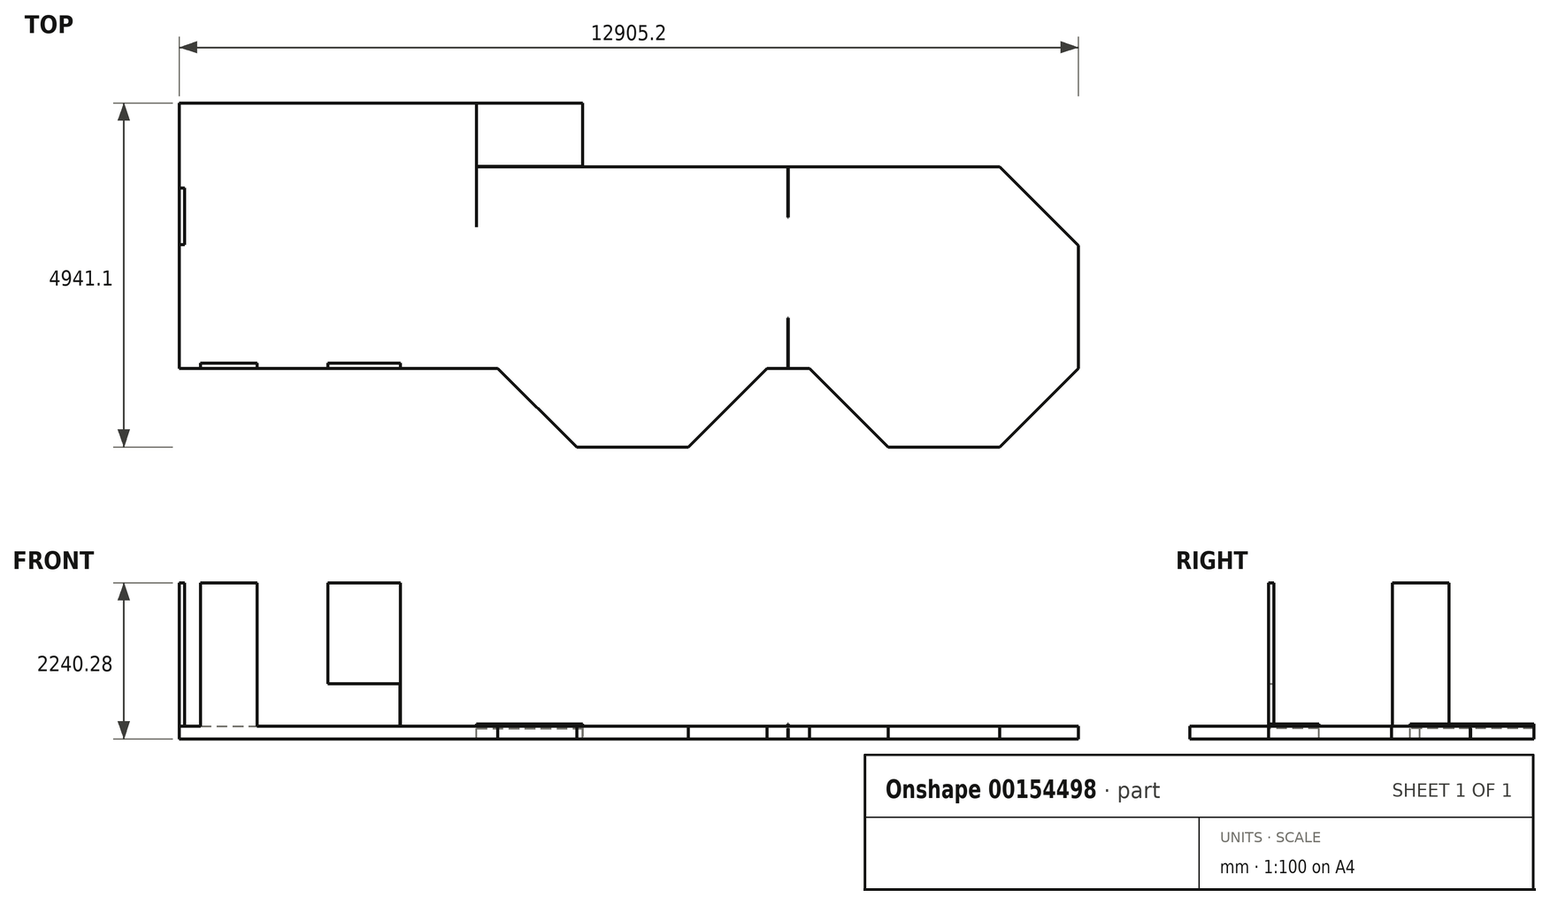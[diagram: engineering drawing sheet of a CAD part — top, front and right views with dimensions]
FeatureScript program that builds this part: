
annotation { "Feature Type Name" : "Feature", "Feature Type Description" : "" }
export const myFeature = defineFeature(function(context is Context, id is Id, definition is map)
    precondition{}
    {
        {
            var Q0;
            Q0=qCreatedBy(makeId("Top.planeOp"),FACE);
            var sketch = newSketch(context, id + "F0", { "sketchPlane" : qUnion([Q0])});
            skLineSegment(sketch, "E0", {"start": v(0, 0) * mm, "end": v(0, 3810) * mm});
            skLineSegment(sketch, "E1", {"start": v(0, 3810) * mm, "end": v(4267.2, 3810) * mm});
            skLineSegment(sketch, "E2", {"start": v(4267.2, 3810) * mm, "end": v(4267.2, 2029.97) * mm});
            skLineSegment(sketch, "E3", {"start": v(4267.2, 2029.97) * mm, "end": v(3352.8, 2029.97) * mm});
            skLineSegment(sketch, "E4", {"start": v(3352.8, 2029.97) * mm, "end": v(3352.8, 0) * mm});
            skLineSegment(sketch, "E5", {"start": v(3352.8, 0) * mm, "end": v(0, 0) * mm});
            skLineSegment(sketch, "E6", {"start": v(4267.2, 3810) * mm, "end": v(5791.2, 3810) * mm});
            skLineSegment(sketch, "E7", {"start": v(5791.2, 3810) * mm, "end": v(5791.2, 2895.6) * mm});
            skLineSegment(sketch, "E8", {"start": v(5791.2, 2895.6) * mm, "end": v(4267.2, 2895.6) * mm});
            skLineSegment(sketch, "E9", {"start": v(0, 3200.4) * mm, "end": v(3352.8, 3200.4) * mm});
            skLineSegment(sketch, "E10", {"start": v(3352.8, 3200.4) * mm, "end": v(3352.8, 3810) * mm});
            skLineSegment(sketch, "E11", {"start": v(4267.2, 2029.97) * mm, "end": v(4267.2, 0) * mm});
            skLineSegment(sketch, "E12", {"start": v(8698.45, 2171.7) * mm, "end": v(8778.78, 2171.7) * mm});
            skLineSegment(sketch, "E13", {"start": v(8778.78, 2171.7) * mm, "end": v(8778.78, 723.9) * mm});
            skLineSegment(sketch, "E14", {"start": v(8778.78, 723.9) * mm, "end": v(8698.45, 723.9) * mm});
            skLineSegment(sketch, "E15", {"start": v(8698.45, 723.9) * mm, "end": v(8698.45, 2171.7) * mm});
            skLineSegment(sketch, "E16", {"start": v(8738.62, 2895.6) * mm, "end": v(11774.13, 2895.6) * mm});
            skLineSegment(sketch, "E17", {"start": v(11774.13, 2895.6) * mm, "end": v(12905.23, 1764.5) * mm});
            skLineSegment(sketch, "E18", {"start": v(12905.23, 1764.5) * mm, "end": v(12905.23, 0) * mm});
            skLineSegment(sketch, "E19", {"start": v(12905.23, 0) * mm, "end": v(11774.13, -1131.1) * mm});
            skLineSegment(sketch, "E20", {"start": v(11774.13, -1131.1) * mm, "end": v(10174.52, -1131.1) * mm});
            skLineSegment(sketch, "E21", {"start": v(8738.62, 0) * mm, "end": v(9043.42, 0) * mm});
            skLineSegment(sketch, "E22", {"start": v(9043.42, 0) * mm, "end": v(10174.52, -1131.1) * mm});
            skLineSegment(sketch, "E23", {"start": v(5791.2, 2895.6) * mm, "end": v(8738.62, 2895.6) * mm});
            skLineSegment(sketch, "E24", {"start": v(4267.2, 0) * mm, "end": v(4572, 0) * mm});
            skLineSegment(sketch, "E25", {"start": v(8738.62, 0) * mm, "end": v(8433.82, 0) * mm});
            skLineSegment(sketch, "E26", {"start": v(4572, 0) * mm, "end": v(5703.1, -1131.1) * mm});
            skLineSegment(sketch, "E27", {"start": v(5703.1, -1131.1) * mm, "end": v(7302.72, -1131.1) * mm});
            skLineSegment(sketch, "E28", {"start": v(7302.72, -1131.1) * mm, "end": v(8433.82, 0) * mm});
            skLineSegment(sketch, "E29", {"start": v(8738.62, 2895.6) * mm, "end": v(8738.62, 2171.7) * mm});
            skLineSegment(sketch, "E30", {"start": v(8738.62, 723.9) * mm, "end": v(8738.62, 0) * mm});
            skLineSegment(sketch, "E31", {"start": v(8738.62, 2994.54) * mm, "end": v(7519.42, 2994.54) * mm});
            skLineSegment(sketch, "E32", {"start": v(7519.42, 2895.6) * mm, "end": v(7519.42, 2994.54) * mm});
            skLineSegment(sketch, "E33", {"start": v(8738.62, 2994.54) * mm, "end": v(9552.43, 2994.54) * mm});
            skLineSegment(sketch, "E34", {"start": v(9552.43, 2895.6) * mm, "end": v(9552.43, 2994.54) * mm});
            skLineSegment(sketch, "E35", {"start": v(10127.42, 2802.52) * mm, "end": v(10127.42, 364.12) * mm});
            skLineSegment(sketch, "E36", {"start": v(10127.42, 364.12) * mm, "end": v(11712.38, 364.12) * mm});
            skLineSegment(sketch, "E37", {"start": v(11712.38, 364.12) * mm, "end": v(11712.38, 2802.52) * mm});
            skLineSegment(sketch, "E38", {"start": v(11712.38, 2802.52) * mm, "end": v(10127.42, 2802.52) * mm});
            skLineSegment(sketch, "E39", {"start": v(-127.81, 2823.67) * mm, "end": v(0, 2823.67) * mm});
            skLineSegment(sketch, "E40", {"start": v(-127.81, 2823.67) * mm, "end": v(-127.81, 2009.85) * mm});
            skLineSegment(sketch, "E41", {"start": v(0, 2009.85) * mm, "end": v(-127.81, 2009.85) * mm});
            skLineSegment(sketch, "E42", {"start": v(304.8, -254.34) * mm, "end": v(304.8, 0) * mm});
            skLineSegment(sketch, "E43", {"start": v(304.8, -254.34) * mm, "end": v(1118.62, -254.34) * mm});
            skLineSegment(sketch, "E44", {"start": v(1118.62, 0) * mm, "end": v(1118.62, -254.34) * mm});
            skLineSegment(sketch, "E45.bottom", {"start": v(1753.67, 1852.42) * mm, "end": v(2668.07, 1852.42) * mm});
            skLineSegment(sketch, "E45.top", {"start": v(1753.67, 328.42) * mm, "end": v(2668.07, 328.42) * mm});
            skLineSegment(sketch, "E45.left", {"start": v(1753.67, 1852.42) * mm, "end": v(1753.67, 328.42) * mm});
            skLineSegment(sketch, "E45.right", {"start": v(2668.07, 1852.42) * mm, "end": v(2668.07, 328.42) * mm});
            skLineSegment(sketch, "E46.bottom", {"start": v(5353.5, 168.2) * mm, "end": v(7639.5, 168.2) * mm});
            skLineSegment(sketch, "E46.top", {"start": v(5353.5, -746.2) * mm, "end": v(7639.5, -746.2) * mm});
            skLineSegment(sketch, "E46.left", {"start": v(5353.5, 168.2) * mm, "end": v(5353.5, -746.2) * mm});
            skLineSegment(sketch, "E46.right", {"start": v(7639.5, 168.2) * mm, "end": v(7639.5, -746.2) * mm});
            skLineSegment(sketch, "E47.bottom", {"start": v(4516.56, 2019.59) * mm, "end": v(5266.98, 1887.27) * mm});
            skLineSegment(sketch, "E47.top", {"start": v(4384.24, 1269.16) * mm, "end": v(5134.66, 1136.84) * mm});
            skLineSegment(sketch, "E47.left", {"start": v(4516.56, 2019.59) * mm, "end": v(4384.24, 1269.16) * mm});
            skLineSegment(sketch, "E47.right", {"start": v(5266.98, 1887.27) * mm, "end": v(5134.66, 1136.84) * mm});
            skLineSegment(sketch, "E48.bottom", {"start": v(4530.69, 90.18) * mm, "end": v(5281.11, 222.5) * mm});
            skLineSegment(sketch, "E48.top", {"start": v(4398.37, 840.6) * mm, "end": v(5148.8, 972.93) * mm});
            skLineSegment(sketch, "E48.left", {"start": v(4530.69, 90.18) * mm, "end": v(4398.37, 840.6) * mm});
            skLineSegment(sketch, "E48.right", {"start": v(5281.11, 222.5) * mm, "end": v(5148.8, 972.93) * mm});
            skCircle(sketch, "E49", {"center": v(5523.92, 1099.62) * mm, "radius": 274.32 * mm});
            skLineSegment(sketch, "E50.bottom", {"start": v(5746.9, 2811.98) * mm, "end": v(7575.7, 2811.98) * mm});
            skLineSegment(sketch, "E50.top", {"start": v(5746.9, 2324.3) * mm, "end": v(7575.7, 2324.3) * mm});
            skLineSegment(sketch, "E50.left", {"start": v(5746.9, 2811.98) * mm, "end": v(5746.9, 2324.3) * mm});
            skLineSegment(sketch, "E50.right", {"start": v(7575.7, 2811.98) * mm, "end": v(7575.7, 2324.3) * mm});
            skLineSegment(sketch, "E51.bottom", {"start": v(5519.63, 2072.82) * mm, "end": v(7958.03, 2072.82) * mm});
            skLineSegment(sketch, "E51.top", {"start": v(5519.63, 396.42) * mm, "end": v(7958.03, 396.42) * mm});
            skLineSegment(sketch, "E51.left", {"start": v(5519.63, 2072.82) * mm, "end": v(5519.63, 396.42) * mm});
            skLineSegment(sketch, "E51.right", {"start": v(7958.03, 2072.82) * mm, "end": v(7958.03, 396.42) * mm});
            skLineSegment(sketch, "E52.bottom", {"start": v(8803.03, 2839.35) * mm, "end": v(9793.63, 2839.35) * mm});
            skLineSegment(sketch, "E52.top", {"start": v(8803.03, 2229.75) * mm, "end": v(9793.63, 2229.75) * mm});
            skLineSegment(sketch, "E52.left", {"start": v(8803.03, 2839.35) * mm, "end": v(8803.03, 2229.75) * mm});
            skLineSegment(sketch, "E52.right", {"start": v(9793.63, 2839.35) * mm, "end": v(9793.63, 2229.75) * mm});
            skLineSegment(sketch, "E53", {"start": v(10127.42, 2522.1) * mm, "end": v(11712.38, 2522.1) * mm});
            skLineSegment(sketch, "E54.bottom", {"start": v(10359.48, -581.46) * mm, "end": v(11670.12, -581.46) * mm});
            skLineSegment(sketch, "E54.top", {"start": v(10359.48, -1038.66) * mm, "end": v(11670.12, -1038.66) * mm});
            skLineSegment(sketch, "E54.left", {"start": v(10359.48, -581.46) * mm, "end": v(10359.48, -1038.66) * mm});
            skLineSegment(sketch, "E54.right", {"start": v(11670.12, -581.46) * mm, "end": v(11670.12, -1038.66) * mm});
            skLineSegment(sketch, "E55.0", {"start": v(8733.62, 2895.6) * mm, "end": v(8733.62, 2171.7) * mm});
            skLineSegment(sketch, "E56.0", {"start": v(8743.62, 2895.6) * mm, "end": v(8743.62, 2171.7) * mm});
            skLineSegment(sketch, "E57.0", {"start": v(4262.2, 3810) * mm, "end": v(4262.2, 2029.97) * mm});
            skLineSegment(sketch, "E58.0", {"start": v(5791.2, 2900.6) * mm, "end": v(4267.2, 2900.6) * mm});
            skLineSegment(sketch, "E59.0", {"start": v(8733.62, 723.9) * mm, "end": v(8733.62, 0) * mm});
            skLineSegment(sketch, "E60.0", {"start": v(8743.62, 723.9) * mm, "end": v(8743.62, 0) * mm});
            skLineSegment(sketch, "E61", {"start": v(3352.8, 0) * mm, "end": v(4267.2, 0) * mm});
            skSolve(sketch);
        }
        {
            var Q0;
            {var subQ0=sQuery(id+"F0.wireOp",EDGE,"E8");Q0=makeQuery(id+"F0.imprint","IMPRINT",FACE,{"disambiguationData":[TD([[makeQuery(id+"F0.imprint","IMPRINT",EDGE,{"derivedFrom":subQ0}),-1.0]])]});}
            var Q1;
            {var subQ4=sQuery(id+"F0.wireOp",EDGE,"E57.0");Q1=makeQuery(id+"F0.imprint","IMPRINT",FACE,{"disambiguationData":[TD([[makeQuery(id+"F0.imprint","IMPRINT",EDGE,{"derivedFrom":subQ4}),1.0]])]});}
            var Q2;
            {var subQ0=sQuery(id+"F0.wireOp",EDGE,"E29");Q2=makeQuery(id+"F0.imprint","IMPRINT",FACE,{"disambiguationData":[TD([[makeQuery(id+"F0.imprint","IMPRINT",EDGE,{"derivedFrom":subQ0}),-1.0]])]});}
            var Q3;
            {var subQ0=sQuery(id+"F0.wireOp",EDGE,"E29");Q3=makeQuery(id+"F0.imprint","IMPRINT",FACE,{"disambiguationData":[TD([[makeQuery(id+"F0.imprint","IMPRINT",EDGE,{"derivedFrom":subQ0}),1.0]])]});}
            var Q4;
            {var subQ0=sQuery(id+"F0.wireOp",EDGE,"E30");Q4=makeQuery(id+"F0.imprint","IMPRINT",FACE,{"disambiguationData":[TD([[makeQuery(id+"F0.imprint","IMPRINT",EDGE,{"derivedFrom":subQ0}),-1.0]])]});}
            var Q5;
            {var subQ0=sQuery(id+"F0.wireOp",EDGE,"E30");Q5=makeQuery(id+"F0.imprint","IMPRINT",FACE,{"disambiguationData":[TD([[makeQuery(id+"F0.imprint","IMPRINT",EDGE,{"derivedFrom":subQ0}),1.0]])]});}
            extrude(context, id + "F1", {"entities" : qUnion([Q0, Q1, Q2, Q3, Q4, Q5]), "depth" : 60.96 * mm});
        }
        {
            var Q0;
            {var subQ5=sQuery(id+"F0.wireOp",EDGE,"E3");Q0=makeQuery(id+"F0.imprint","IMPRINT",FACE,{"disambiguationData":[TD([[makeQuery(id+"F0.imprint","IMPRINT",EDGE,{"derivedFrom":subQ5}),-1.0]])]});}
            var Q1;
            {var subQ3=sQuery(id+"F0.wireOp",EDGE,"E9");Q1=makeQuery(id+"F0.imprint","IMPRINT",FACE,{"disambiguationData":[TD([[makeQuery(id+"F0.imprint","IMPRINT",EDGE,{"derivedFrom":subQ3}),1.0]])]});}
            var Q2;
            Q2=makeQuery(id+"F0.imprint","IMPRINT",FACE,{"disambiguationData":[TD([[makeQuery(id+"F0.imprint","IMPRINT",EDGE,{"derivedFrom":sQuery(id+"F0.wireOp",EDGE,"E45.bottom")}),-1.0]])]});
            var Q3;
            {var subQ6=sQuery(id+"F0.wireOp",EDGE,"E8");Q3=makeQuery(id+"F0.imprint","IMPRINT",FACE,{"disambiguationData":[TD([[makeQuery(id+"F0.imprint","IMPRINT",EDGE,{"derivedFrom":subQ6}),1.0]])]});}
            var Q4;
            {var subQ0=sQuery(id+"F0.wireOp",EDGE,"E6");Q4=makeQuery(id+"F0.imprint","IMPRINT",FACE,{"disambiguationData":[TD([[makeQuery(id+"F0.imprint","IMPRINT",EDGE,{"derivedFrom":subQ0}),-1.0]])]});}
            var Q5;
            Q5=makeQuery(id+"F0.imprint","IMPRINT",FACE,{"disambiguationData":[TD([[makeQuery(id+"F0.imprint","IMPRINT",EDGE,{"derivedFrom":sQuery(id+"F0.wireOp",EDGE,"E50.bottom")}),-1.0]])]});
            var Q6;
            {var subQ1=sQuery(id+"F0.wireOp",EDGE,"E51.bottom");Q6=makeQuery(id+"F0.imprint","IMPRINT",FACE,{"disambiguationData":[TD([[makeQuery(id+"F0.imprint","IMPRINT",EDGE,{"derivedFrom":subQ1}),-1.0]])]});}
            var Q7;
            Q7=makeQuery(id+"F0.imprint","IMPRINT",FACE,{"disambiguationData":[TD([[makeQuery(id+"F0.imprint","IMPRINT",EDGE,{"derivedFrom":sQuery(id+"F0.wireOp",EDGE,"E46.bottom")}),-1.0]])]});
            var Q8;
            Q8=makeQuery(id+"F0.imprint","IMPRINT",FACE,{"disambiguationData":[TD([[makeQuery(id+"F0.imprint","IMPRINT",EDGE,{"derivedFrom":sQuery(id+"F0.wireOp",EDGE,"E48.bottom")}),1.0]])]});
            var Q9;
            Q9=makeQuery(id+"F0.imprint","IMPRINT",FACE,{"disambiguationData":[TD([[makeQuery(id+"F0.imprint","IMPRINT",EDGE,{"derivedFrom":sQuery(id+"F0.wireOp",EDGE,"E47.bottom")}),-1.0]])]});
            var Q10;
            {var subQ0=sQuery(id+"F0.wireOp",EDGE,"E51.left");var subQ1=sQuery(id+"F0.wireOp",EDGE,"E49");var subQ2=makeQuery(id+"F0.imprint","INTERSECT",VERTEX,{"disambiguationData":[OD(0.0)],"derivedFrom":[subQ1,subQ0]});Q10=makeQuery(id+"F0.imprint","IMPRINT",FACE,{"disambiguationData":[TD([[makeQuery(id+"F0.imprint","IMPRINT",EDGE,{"disambiguationData":[TD([[subQ2,-1.0]])],"derivedFrom":subQ1}),1.0]])]});}
            var Q11;
            {var subQ0=sQuery(id+"F0.wireOp",EDGE,"E51.left");var subQ1=sQuery(id+"F0.wireOp",EDGE,"E49");var subQ2=makeQuery(id+"F0.imprint","INTERSECT",VERTEX,{"disambiguationData":[OD(0.0)],"derivedFrom":[subQ1,subQ0]});Q11=makeQuery(id+"F0.imprint","IMPRINT",FACE,{"disambiguationData":[TD([[makeQuery(id+"F0.imprint","IMPRINT",EDGE,{"disambiguationData":[TD([[subQ2,1.0]])],"derivedFrom":subQ1}),1.0]])]});}
            var Q12;
            {var subQ13=sQuery(id+"F0.wireOp",EDGE,"E13");Q12=makeQuery(id+"F0.imprint","IMPRINT",FACE,{"disambiguationData":[TD([[makeQuery(id+"F0.imprint","IMPRINT",EDGE,{"derivedFrom":subQ13}),1.0]])]});}
            var Q13;
            {var subQ0=sQuery(id+"F0.wireOp",EDGE,"E36");Q13=makeQuery(id+"F0.imprint","IMPRINT",FACE,{"disambiguationData":[TD([[makeQuery(id+"F0.imprint","IMPRINT",EDGE,{"derivedFrom":subQ0}),1.0]])]});}
            var Q14;
            {var subQ0=sQuery(id+"F0.wireOp",EDGE,"E38");Q14=makeQuery(id+"F0.imprint","IMPRINT",FACE,{"disambiguationData":[TD([[makeQuery(id+"F0.imprint","IMPRINT",EDGE,{"derivedFrom":subQ0}),1.0]])]});}
            var Q15;
            Q15=makeQuery(id+"F0.imprint","IMPRINT",FACE,{"disambiguationData":[TD([[makeQuery(id+"F0.imprint","IMPRINT",EDGE,{"derivedFrom":sQuery(id+"F0.wireOp",EDGE,"E54.bottom")}),-1.0]])]});
            var Q16;
            Q16=makeQuery(id+"F0.imprint","IMPRINT",FACE,{"disambiguationData":[TD([[makeQuery(id+"F0.imprint","IMPRINT",EDGE,{"derivedFrom":sQuery(id+"F0.wireOp",EDGE,"E52.bottom")}),-1.0]])]});
            var Q17;
            {var subQ1=sQuery(id+"F0.wireOp",EDGE,"E13");Q17=makeQuery(id+"F0.imprint","IMPRINT",FACE,{"disambiguationData":[TD([[makeQuery(id+"F0.imprint","IMPRINT",EDGE,{"derivedFrom":subQ1}),-1.0]])]});}
            var Q18;
            {var subQ6=sQuery(id+"F0.wireOp",EDGE,"E4");Q18=makeQuery(id+"F0.imprint","IMPRINT",FACE,{"disambiguationData":[TD([[makeQuery(id+"F0.imprint","IMPRINT",EDGE,{"derivedFrom":subQ6}),-1.0]])]});}
            var Q19;
            {var subQ0=sQuery(id+"F0.wireOp",EDGE,"E8");Q19=makeQuery(id+"F0.imprint","IMPRINT",FACE,{"disambiguationData":[TD([[makeQuery(id+"F0.imprint","IMPRINT",EDGE,{"derivedFrom":subQ0}),-1.0]])]});}
            var Q20;
            {var subQ0=sQuery(id+"F0.wireOp",EDGE,"E30");Q20=makeQuery(id+"F0.imprint","IMPRINT",FACE,{"disambiguationData":[TD([[makeQuery(id+"F0.imprint","IMPRINT",EDGE,{"derivedFrom":subQ0}),-1.0]])]});}
            var Q21;
            {var subQ0=sQuery(id+"F0.wireOp",EDGE,"E30");Q21=makeQuery(id+"F0.imprint","IMPRINT",FACE,{"disambiguationData":[TD([[makeQuery(id+"F0.imprint","IMPRINT",EDGE,{"derivedFrom":subQ0}),1.0]])]});}
            var Q22;
            {var subQ0=sQuery(id+"F0.wireOp",EDGE,"E29");Q22=makeQuery(id+"F0.imprint","IMPRINT",FACE,{"disambiguationData":[TD([[makeQuery(id+"F0.imprint","IMPRINT",EDGE,{"derivedFrom":subQ0}),1.0]])]});}
            var Q23;
            {var subQ0=sQuery(id+"F0.wireOp",EDGE,"E29");Q23=makeQuery(id+"F0.imprint","IMPRINT",FACE,{"disambiguationData":[TD([[makeQuery(id+"F0.imprint","IMPRINT",EDGE,{"derivedFrom":subQ0}),-1.0]])]});}
            extrude(context, id + "F2", {"entities" : qUnion([Q0, Q1, Q2, Q3, Q4, Q5, Q6, Q7, Q8, Q9, Q10, Q11, Q12, Q13, Q14, Q15, Q16, Q17, Q18, Q19, Q20, Q21, Q22, Q23]), "depth" : 30.48 * mm});
        }
        {
            var Q0;
            Q0=makeQuery(id+"F1.opExtrude","SWEPT_BODY",BODY,{"disambiguationData":[OSD([sQuery(id+"F0.wireOp",EDGE,"E1"),sQuery(id+"F0.wireOp",EDGE,"E2"),sQuery(id+"F0.wireOp",EDGE,"E3"),sQuery(id+"F0.wireOp",EDGE,"E7"),sQuery(id+"F0.wireOp",EDGE,"E8"),sQuery(id+"F0.wireOp",EDGE,"E57.0"),sQuery(id+"F0.wireOp",EDGE,"E58.0")])]});
            var Q1;
            Q1=makeQuery(id+"F1.opExtrude","SWEPT_BODY",BODY,{"disambiguationData":[OSD([sQuery(id+"F0.wireOp",EDGE,"E12"),sQuery(id+"F0.wireOp",EDGE,"E16"),sQuery(id+"F0.wireOp",EDGE,"E23"),sQuery(id+"F0.wireOp",EDGE,"E55.0"),sQuery(id+"F0.wireOp",EDGE,"E56.0")])]});
            var Q2;
            Q2=makeQuery(id+"F1.opExtrude","SWEPT_BODY",BODY,{"disambiguationData":[OSD([sQuery(id+"F0.wireOp",EDGE,"E14"),sQuery(id+"F0.wireOp",EDGE,"E21"),sQuery(id+"F0.wireOp",EDGE,"E25"),sQuery(id+"F0.wireOp",EDGE,"E59.0"),sQuery(id+"F0.wireOp",EDGE,"E60.0")])]});
            var Q3;
            Q3=makeQuery(id+"F2.opExtrude","SWEPT_BODY",BODY,{"disambiguationData":[OSD([sQuery(id+"F0.wireOp",EDGE,"E0"),sQuery(id+"F0.wireOp",EDGE,"E1"),sQuery(id+"F0.wireOp",EDGE,"E3"),sQuery(id+"F0.wireOp",EDGE,"E4"),sQuery(id+"F0.wireOp",EDGE,"E5"),sQuery(id+"F0.wireOp",EDGE,"E6"),sQuery(id+"F0.wireOp",EDGE,"E7"),sQuery(id+"F0.wireOp",EDGE,"E11"),sQuery(id+"F0.wireOp",EDGE,"E16"),sQuery(id+"F0.wireOp",EDGE,"E17"),sQuery(id+"F0.wireOp",EDGE,"E18"),sQuery(id+"F0.wireOp",EDGE,"E19"),sQuery(id+"F0.wireOp",EDGE,"E20"),sQuery(id+"F0.wireOp",EDGE,"E21"),sQuery(id+"F0.wireOp",EDGE,"E22"),sQuery(id+"F0.wireOp",EDGE,"E23"),sQuery(id+"F0.wireOp",EDGE,"E24"),sQuery(id+"F0.wireOp",EDGE,"E25"),sQuery(id+"F0.wireOp",EDGE,"E26"),sQuery(id+"F0.wireOp",EDGE,"E27"),sQuery(id+"F0.wireOp",EDGE,"E28")])]});
            booleanBodies(context, id + "F3", {"operationType" : BooleanOperationType.UNION, "tools" : qUnion([Q0, Q1, Q2, Q3])});
        }
        {
            var Q0;
            {var subQ0=sQuery(id+"F0.wireOp",EDGE,"E4");var subQ1=sQuery(id+"F0.wireOp",EDGE,"E0");var subQ2=sQuery(id+"F0.wireOp",EDGE,"E3");var subQ3=sQuery(id+"F0.wireOp",EDGE,"E1");var subQ4=sQuery(id+"F0.wireOp",EDGE,"E6");var subQ5=sQuery(id+"F0.wireOp",EDGE,"E5");Q0=makeQuery(id+"F3.opBoolean","SPLIT",FACE,{"disambiguationData":[TD([makeQuery(id+"F1.opExtrude","SWEPT_FACE",FACE,{"disambiguationData":[OSD([sQuery(id+"F0.wireOp",EDGE,"E57.0")])]})])],"derivedFrom":makeQuery(id+"F2.opExtrude","CAP_FACE",FACE,{"disambiguationData":[OSD([subQ1,subQ3,subQ2,subQ0,subQ5,subQ4,sQuery(id+"F0.wireOp",EDGE,"E7"),sQuery(id+"F0.wireOp",EDGE,"E11"),sQuery(id+"F0.wireOp",EDGE,"E16"),sQuery(id+"F0.wireOp",EDGE,"E17"),sQuery(id+"F0.wireOp",EDGE,"E18"),sQuery(id+"F0.wireOp",EDGE,"E19"),sQuery(id+"F0.wireOp",EDGE,"E20"),sQuery(id+"F0.wireOp",EDGE,"E21"),sQuery(id+"F0.wireOp",EDGE,"E22"),sQuery(id+"F0.wireOp",EDGE,"E23"),sQuery(id+"F0.wireOp",EDGE,"E24"),sQuery(id+"F0.wireOp",EDGE,"E25"),sQuery(id+"F0.wireOp",EDGE,"E26"),sQuery(id+"F0.wireOp",EDGE,"E27"),sQuery(id+"F0.wireOp",EDGE,"E28")])],"isStart":false})});}
            var sketch = newSketch(context, id + "F4", { "sketchPlane" : qUnion([Q0])});
            skLineSegment(sketch, "E62.bottom", {"start": v(0, 2590.8) * mm, "end": v(76.2, 2590.8) * mm});
            skLineSegment(sketch, "E62.top", {"start": v(0, 1778) * mm, "end": v(76.2, 1778) * mm});
            skLineSegment(sketch, "E62.left", {"start": v(0, 2590.8) * mm, "end": v(0, 1778) * mm});
            skLineSegment(sketch, "E62.right", {"start": v(76.2, 2590.8) * mm, "end": v(76.2, 1778) * mm});
            skLineSegment(sketch, "E63.bottom", {"start": v(304.8, 0) * mm, "end": v(1117.6, 0) * mm});
            skLineSegment(sketch, "E63.top", {"start": v(304.8, 76.2) * mm, "end": v(1117.6, 76.2) * mm});
            skLineSegment(sketch, "E63.left", {"start": v(304.8, 0) * mm, "end": v(304.8, 76.2) * mm});
            skLineSegment(sketch, "E63.right", {"start": v(1117.6, 0) * mm, "end": v(1117.6, 76.2) * mm});
            skLineSegment(sketch, "E64.bottom", {"start": v(2133.6, 0) * mm, "end": v(3169.92, 0) * mm});
            skLineSegment(sketch, "E64.top", {"start": v(2133.6, 76.2) * mm, "end": v(3169.92, 76.2) * mm});
            skLineSegment(sketch, "E64.left", {"start": v(2133.6, 0) * mm, "end": v(2133.6, 76.2) * mm});
            skLineSegment(sketch, "E64.right", {"start": v(3169.92, 0) * mm, "end": v(3169.92, 76.2) * mm});
            skSolve(sketch);
        }
        {
            var Q0;
            Q0=makeQuery(id+"F4.imprint","IMPRINT",FACE,{"disambiguationData":[TD([[makeQuery(id+"F4.imprint","IMPRINT",EDGE,{"derivedFrom":sQuery(id+"F4.wireOp",EDGE,"E62.bottom")}),-1.0]])]});
            var Q1;
            Q1=makeQuery(id+"F4.imprint","IMPRINT",FACE,{"disambiguationData":[TD([[makeQuery(id+"F4.imprint","IMPRINT",EDGE,{"derivedFrom":sQuery(id+"F4.wireOp",EDGE,"E63.bottom")}),-1.0]])]});
            var Q2;
            Q2=makeQuery(id+"F4.imprint","IMPRINT",FACE,{"disambiguationData":[TD([[makeQuery(id+"F4.imprint","IMPRINT",EDGE,{"derivedFrom":sQuery(id+"F4.wireOp",EDGE,"E64.bottom")}),-1.0]])]});
            extrude(context, id + "F5", {"entities" : qUnion([Q0, Q1, Q2]), "operationType" : NewBodyOperationType.ADD, "depth" : 2057.4 * mm});
        }
        {
            var Q0;
            Q0=makeQuery(id+"F5.opExtrude","SWEPT_FACE",FACE,{"disambiguationData":[OSD([sQuery(id+"F4.wireOp",EDGE,"E64.top")])]});
            var sketch = newSketch(context, id + "F6", { "sketchPlane" : qUnion([Q0])});
            skLineSegment(sketch, "E65.bottom", {"start": v(-3169.92, 30.48) * mm, "end": v(-2133.6, 30.48) * mm});
            skLineSegment(sketch, "E65.top", {"start": v(-3167.38, 640.08) * mm, "end": v(-2133.6, 640.08) * mm});
            skLineSegment(sketch, "E65.left", {"start": v(-3167.38, 30.48) * mm, "end": v(-3167.38, 640.08) * mm});
            skLineSegment(sketch, "E65.right", {"start": v(-2133.6, 30.48) * mm, "end": v(-2133.6, 640.08) * mm});
            skSolve(sketch);
        }
        {
            var Q0;
            Q0=makeQuery(id+"F6.imprint","IMPRINT",FACE,{"disambiguationData":[TD([[makeQuery(id+"F6.imprint","IMPRINT",EDGE,{"derivedFrom":sQuery(id+"F6.wireOp",EDGE,"E65.bottom")}),-1.0]])]});
            extrude(context, id + "F7", {"entities" : qUnion([Q0]), "operationType" : NewBodyOperationType.REMOVE, "endBound" : BoundingType.THROUGH_ALL, "oppositeDirection" : true, "depth" : 30.48 * mm});
        }
        {
            var Q0;
            {var subQ6=sQuery(id+"F0.wireOp",EDGE,"E4");Q0=makeQuery(id+"F0.imprint","IMPRINT",FACE,{"disambiguationData":[TD([[makeQuery(id+"F0.imprint","IMPRINT",EDGE,{"derivedFrom":subQ6}),-1.0]])]});}
            var Q1;
            {var subQ3=sQuery(id+"F0.wireOp",EDGE,"E9");Q1=makeQuery(id+"F0.imprint","IMPRINT",FACE,{"disambiguationData":[TD([[makeQuery(id+"F0.imprint","IMPRINT",EDGE,{"derivedFrom":subQ3}),1.0]])]});}
            var Q2;
            Q2=makeQuery(id+"F0.imprint","IMPRINT",FACE,{"disambiguationData":[TD([[makeQuery(id+"F0.imprint","IMPRINT",EDGE,{"derivedFrom":sQuery(id+"F0.wireOp",EDGE,"E45.bottom")}),-1.0]])]});
            var Q3;
            {var subQ8=sQuery(id+"F0.wireOp",EDGE,"E8");Q3=makeQuery(id+"F0.imprint","IMPRINT",FACE,{"disambiguationData":[TD([[makeQuery(id+"F0.imprint","IMPRINT",EDGE,{"derivedFrom":subQ8}),1.0]])]});}
            var Q4;
            Q4=makeQuery(id+"F0.imprint","IMPRINT",FACE,{"disambiguationData":[TD([[makeQuery(id+"F0.imprint","IMPRINT",EDGE,{"derivedFrom":sQuery(id+"F0.wireOp",EDGE,"E48.bottom")}),1.0]])]});
            var Q5;
            Q5=makeQuery(id+"F0.imprint","IMPRINT",FACE,{"disambiguationData":[TD([[makeQuery(id+"F0.imprint","IMPRINT",EDGE,{"derivedFrom":sQuery(id+"F0.wireOp",EDGE,"E47.bottom")}),-1.0]])]});
            var Q6;
            {var subQ1=sQuery(id+"F0.wireOp",EDGE,"E51.bottom");Q6=makeQuery(id+"F0.imprint","IMPRINT",FACE,{"disambiguationData":[TD([[makeQuery(id+"F0.imprint","IMPRINT",EDGE,{"derivedFrom":subQ1}),-1.0]])]});}
            var Q7;
            Q7=makeQuery(id+"F0.imprint","IMPRINT",FACE,{"disambiguationData":[TD([[makeQuery(id+"F0.imprint","IMPRINT",EDGE,{"derivedFrom":sQuery(id+"F0.wireOp",EDGE,"E46.bottom")}),-1.0]])]});
            var Q8;
            Q8=makeQuery(id+"F0.imprint","IMPRINT",FACE,{"disambiguationData":[TD([[makeQuery(id+"F0.imprint","IMPRINT",EDGE,{"derivedFrom":sQuery(id+"F0.wireOp",EDGE,"E50.bottom")}),-1.0]])]});
            var Q9;
            {var subQ0=sQuery(id+"F0.wireOp",EDGE,"E6");Q9=makeQuery(id+"F0.imprint","IMPRINT",FACE,{"disambiguationData":[TD([[makeQuery(id+"F0.imprint","IMPRINT",EDGE,{"derivedFrom":subQ0}),-1.0]])]});}
            var Q10;
            {var subQ0=sQuery(id+"F0.wireOp",EDGE,"E51.left");var subQ1=sQuery(id+"F0.wireOp",EDGE,"E49");var subQ2=makeQuery(id+"F0.imprint","INTERSECT",VERTEX,{"disambiguationData":[OD(0.0)],"derivedFrom":[subQ1,subQ0]});Q10=makeQuery(id+"F0.imprint","IMPRINT",FACE,{"disambiguationData":[TD([[makeQuery(id+"F0.imprint","IMPRINT",EDGE,{"disambiguationData":[TD([[subQ2,1.0]])],"derivedFrom":subQ1}),1.0]])]});}
            var Q11;
            {var subQ0=sQuery(id+"F0.wireOp",EDGE,"E51.left");var subQ1=sQuery(id+"F0.wireOp",EDGE,"E49");var subQ2=makeQuery(id+"F0.imprint","INTERSECT",VERTEX,{"disambiguationData":[OD(0.0)],"derivedFrom":[subQ1,subQ0]});Q11=makeQuery(id+"F0.imprint","IMPRINT",FACE,{"disambiguationData":[TD([[makeQuery(id+"F0.imprint","IMPRINT",EDGE,{"disambiguationData":[TD([[subQ2,-1.0]])],"derivedFrom":subQ1}),1.0]])]});}
            var Q12;
            {var subQ11=sQuery(id+"F0.wireOp",EDGE,"E13");Q12=makeQuery(id+"F0.imprint","IMPRINT",FACE,{"disambiguationData":[TD([[makeQuery(id+"F0.imprint","IMPRINT",EDGE,{"derivedFrom":subQ11}),1.0]])]});}
            var Q13;
            {var subQ0=sQuery(id+"F0.wireOp",EDGE,"E36");Q13=makeQuery(id+"F0.imprint","IMPRINT",FACE,{"disambiguationData":[TD([[makeQuery(id+"F0.imprint","IMPRINT",EDGE,{"derivedFrom":subQ0}),1.0]])]});}
            var Q14;
            Q14=makeQuery(id+"F0.imprint","IMPRINT",FACE,{"disambiguationData":[TD([[makeQuery(id+"F0.imprint","IMPRINT",EDGE,{"derivedFrom":sQuery(id+"F0.wireOp",EDGE,"E54.bottom")}),-1.0]])]});
            var Q15;
            {var subQ0=sQuery(id+"F0.wireOp",EDGE,"E38");Q15=makeQuery(id+"F0.imprint","IMPRINT",FACE,{"disambiguationData":[TD([[makeQuery(id+"F0.imprint","IMPRINT",EDGE,{"derivedFrom":subQ0}),1.0]])]});}
            var Q16;
            Q16=makeQuery(id+"F0.imprint","IMPRINT",FACE,{"disambiguationData":[TD([[makeQuery(id+"F0.imprint","IMPRINT",EDGE,{"derivedFrom":sQuery(id+"F0.wireOp",EDGE,"E52.bottom")}),-1.0]])]});
            var Q17;
            {var subQ0=sQuery(id+"F0.wireOp",EDGE,"E13");Q17=makeQuery(id+"F0.imprint","IMPRINT",FACE,{"disambiguationData":[TD([[makeQuery(id+"F0.imprint","IMPRINT",EDGE,{"derivedFrom":subQ0}),-1.0]])]});}
            extrude(context, id + "F8", {"entities" : qUnion([Q0, Q1, Q2, Q3, Q4, Q5, Q6, Q7, Q8, Q9, Q10, Q11, Q12, Q13, Q14, Q15, Q16, Q17]), "operationType" : NewBodyOperationType.ADD, "oppositeDirection" : true, "depth" : 152.4 * mm});
        }
        {
            var Q0;
            {var subQ1=sQuery(id+"F0.wireOp",EDGE,"E4");Q0=makeQuery(id+"F0.imprint","IMPRINT",FACE,{"disambiguationData":[TD([[makeQuery(id+"F0.imprint","IMPRINT",EDGE,{"derivedFrom":subQ1}),1.0]])]});}
            extrude(context, id + "F9", {"entities" : qUnion([Q0]), "operationType" : NewBodyOperationType.ADD, "oppositeDirection" : true, "depth" : 152.4 * mm, "hasSecondDirection" : true, "secondDirectionOppositeDirection" : false, "secondDirectionDepth" : 30.48 * mm});
        }
    });
